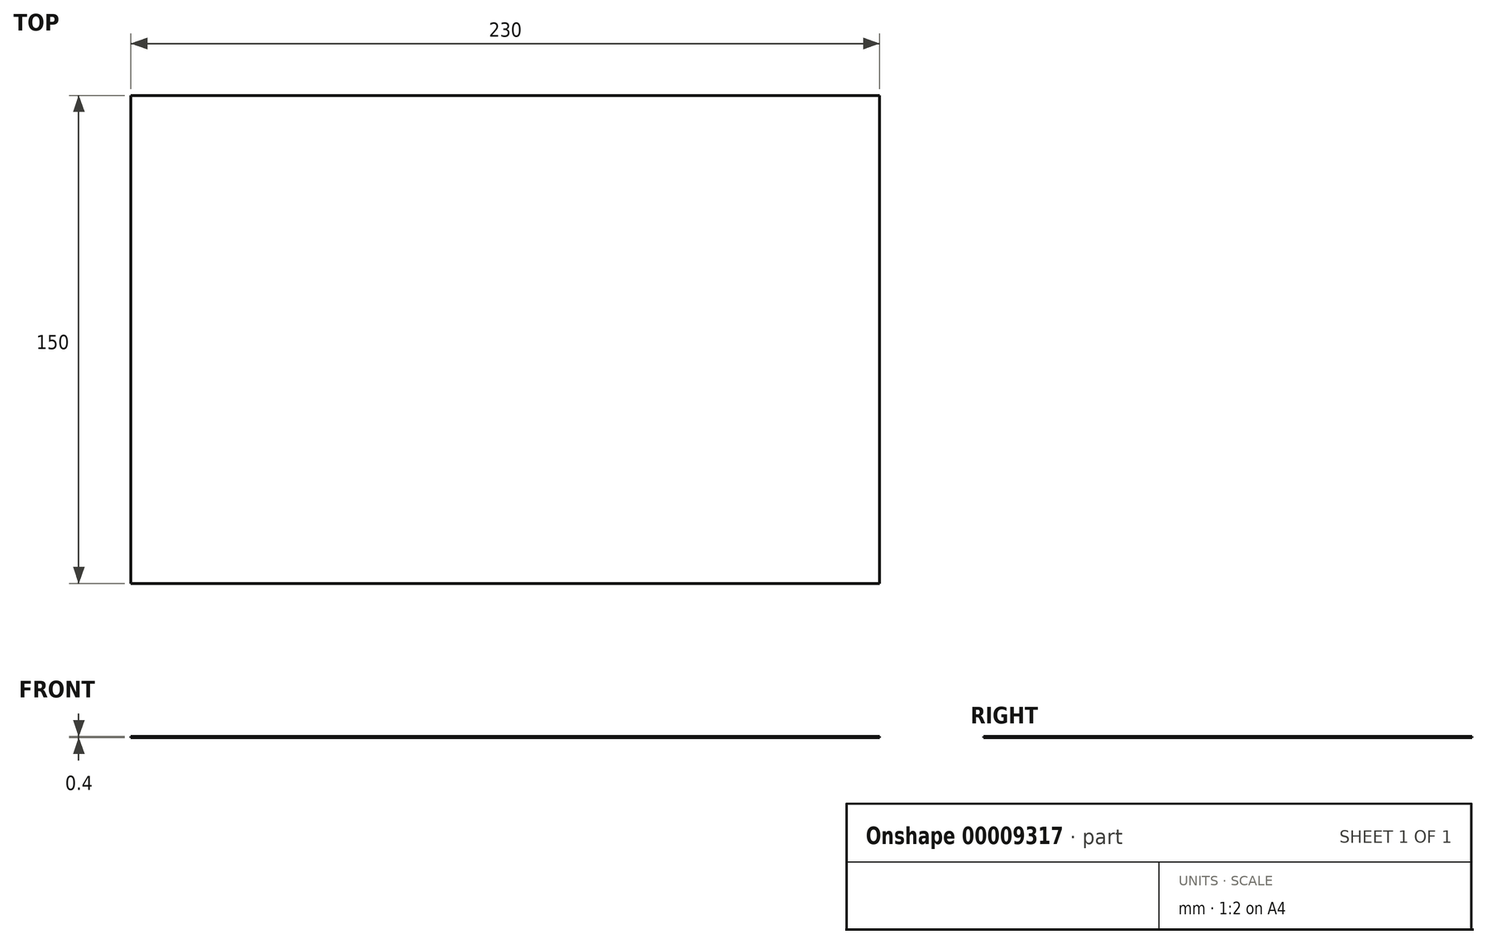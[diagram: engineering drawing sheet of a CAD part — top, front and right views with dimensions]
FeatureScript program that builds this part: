
annotation { "Feature Type Name" : "Feature", "Feature Type Description" : "" }
export const myFeature = defineFeature(function(context is Context, id is Id, definition is map)
    precondition{}
    {
        {
            var Q0;
            Q0=qCreatedBy(makeId("Top.planeOp"),FACE);
            var sketch = newSketch(context, id + "F0", { "sketchPlane" : qUnion([Q0])});
            skLineSegment(sketch, "E0.bottom", {"start": v(-115, -75) * mm, "end": v(115, -75) * mm});
            skLineSegment(sketch, "E0.top", {"start": v(-115, 75) * mm, "end": v(115, 75) * mm});
            skLineSegment(sketch, "E0.left", {"start": v(-115, -75) * mm, "end": v(-115, 75) * mm});
            skLineSegment(sketch, "E0.right", {"start": v(115, -75) * mm, "end": v(115, 75) * mm});
            skPoint(sketch, "E1", {"position": v(0, 75) * mm});
            skPoint(sketch, "E2", {"position": v(-115, 0) * mm});
            skSolve(sketch);
        }
        {
            var Q0;
            Q0=makeQuery(id+"F0.imprint","IMPRINT",FACE,{"disambiguationData":[TD([[makeQuery(id+"F0.imprint","IMPRINT",EDGE,{"derivedFrom":sQuery(id+"F0.wireOp",EDGE,"E0.bottom")}),1.0]])]});
            extrude(context, id + "F1", {"entities" : qUnion([Q0]), "depth" : .4 * mm});
        }
    });
